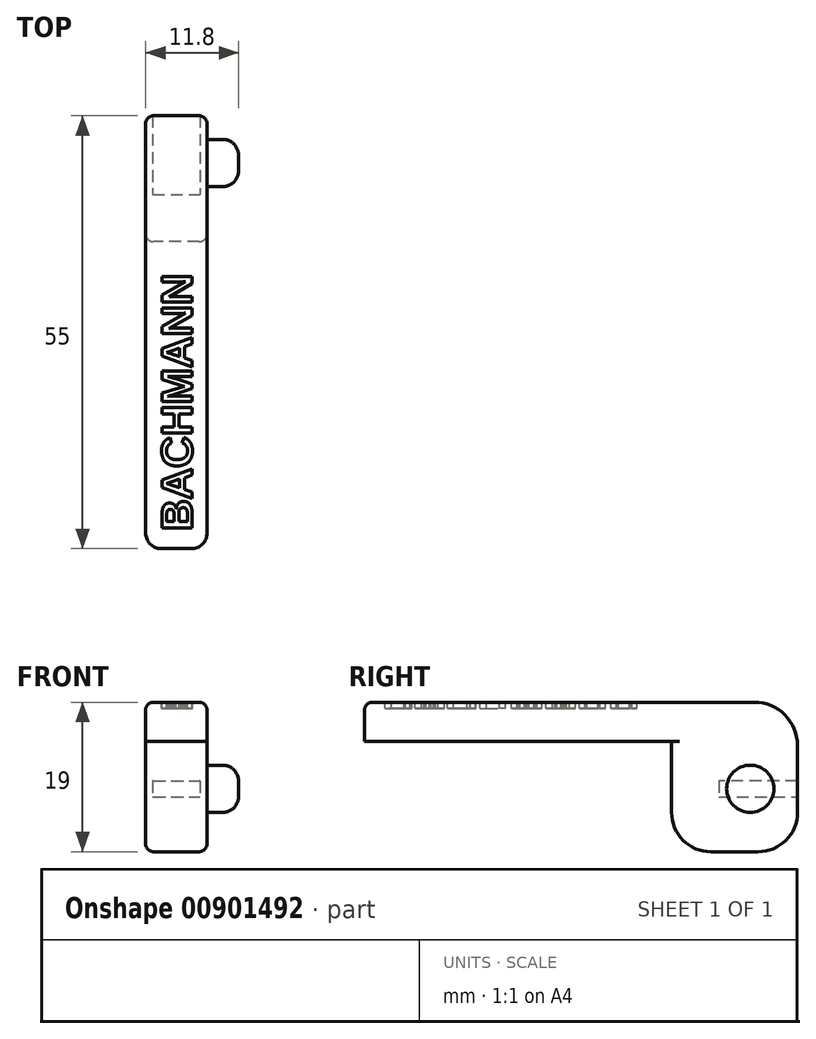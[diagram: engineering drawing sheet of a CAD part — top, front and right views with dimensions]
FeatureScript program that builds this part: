
annotation { "Feature Type Name" : "Feature", "Feature Type Description" : "" }
export const myFeature = defineFeature(function(context is Context, id is Id, definition is map)
    precondition{}
    {
        {
            var Q0;
            Q0=qCreatedBy(makeId("Right.planeOp"),FACE);
            var sketch = newSketch(context, id + "F0", { "sketchPlane" : qUnion([Q0])});
            skLineSegment(sketch, "E0", {"start": v(0, 0) * mm, "end": v(39, 0) * mm});
            skLineSegment(sketch, "E1", {"start": v(39, 0) * mm, "end": v(0, 0) * mm});
            skLineSegment(sketch, "E2", {"start": v(0, 0) * mm, "end": v(0, 5) * mm});
            skLineSegment(sketch, "E3", {"start": v(0, 5) * mm, "end": v(55, 5) * mm});
            skLineSegment(sketch, "E4", {"start": v(55, 5) * mm, "end": v(55, -14) * mm});
            skLineSegment(sketch, "E5", {"start": v(55, -14) * mm, "end": v(39, -14) * mm});
            skLineSegment(sketch, "E6", {"start": v(39, -14) * mm, "end": v(39, 0) * mm});
            skSolve(sketch);
        }
        {
            var Q0;
            Q0 = qSketchRegion(id + "F0", true);
            extrude(context, id + "F1", {"entities" : qUnion([Q0]), "endBound" : BoundingType.SYMMETRIC, "depth" : 7.8 * mm, "offsetDistance" : 25 * mm});
        }
        {
            var Q0;
            Q0=qCreatedBy(makeId("Right.planeOp"),FACE);
            var sketch = newSketch(context, id + "F2", { "sketchPlane" : qUnion([Q0])});
            skLineSegment(sketch, "E7.0", {"start": v(55, 5) * mm, "end": v(55, -14) * mm});
            skLineSegment(sketch, "E8", {"start": v(55, -5) * mm, "end": v(45, -5) * mm});
            skLineSegment(sketch, "E9", {"start": v(45, -5) * mm, "end": v(45, -7) * mm});
            skLineSegment(sketch, "E10", {"start": v(45, -7) * mm, "end": v(55, -7) * mm});
            skSolve(sketch);
        }
        {
            var Q0;
            Q0 = qSketchRegion(id + "F2", true);
            extrude(context, id + "F3", {"entities" : qUnion([Q0]), "operationType" : NewBodyOperationType.REMOVE, "endBound" : BoundingType.SYMMETRIC, "oppositeDirection" : true, "depth" : 6 * mm, "offsetDistance" : 25 * mm});
        }
        {
            var Q0;
            Q0=makeQuery(id+"F1.opExtrude","SWEPT_FACE",FACE,{"disambiguationData":[OSD([sQuery(id+"F0.wireOp",EDGE,"E3")])]});
            var sketch = newSketch(context, id + "F4", { "sketchPlane" : qUnion([Q0])});
            skText(sketch, "E11", { "text": "BACHMANN", "fontName": "Arimo-Bold.ttf"});
            const initialGuessF4  = {"E11": [0.002, 0.00226, 0, 1, 0.004]};
            skSetInitialGuess(sketch, initialGuessF4);
            skSolve(sketch);
        }
        {
            var Q0;
            Q0=makeQuery(id+"F1.opExtrude","CAP_FACE",FACE,{"disambiguationData":[OSD([sQuery(id+"F0.wireOp",EDGE,"E1"),sQuery(id+"F0.wireOp",EDGE,"E2"),sQuery(id+"F0.wireOp",EDGE,"E3"),sQuery(id+"F0.wireOp",EDGE,"E4"),sQuery(id+"F0.wireOp",EDGE,"E5"),sQuery(id+"F0.wireOp",EDGE,"E6")])],"isStart":false});
            var sketch = newSketch(context, id + "F5", { "sketchPlane" : qUnion([Q0])});
            skCircle(sketch, "E12", {"center": v(49, -6) * mm, "radius": 3 * mm});
            skSolve(sketch);
        }
        {
            var Q0;
            Q0 = qSketchRegion(id + "F5", true);
            extrude(context, id + "F6", {"entities" : qUnion([Q0]), "operationType" : NewBodyOperationType.ADD, "depth" : 4 * mm, "offsetDistance" : 25 * mm});
        }
        {
            var Q0;
            Q0 = qSketchRegion(id + "F4", true);
            extrude(context, id + "F7", {"entities" : qUnion([Q0]), "operationType" : NewBodyOperationType.REMOVE, "oppositeDirection" : true, "depth" : .8 * mm, "offsetDistance" : 25 * mm});
        }
        {
            var Q0;
            {var subQ0=sQuery(id+"F0.wireOp",EDGE,"E2");var subQ4=sQuery(id+"F0.wireOp",EDGE,"E3");Q0=makeQuery(id+"F7.boolean.opBoolean","SPLIT",FACE,{"disambiguationData":[TD([makeQuery(id+"F1.opExtrude","SWEPT_FACE",FACE,{"disambiguationData":[OSD([subQ0])]})])],"derivedFrom":makeQuery(id+"F1.opExtrude","SWEPT_FACE",FACE,{"disambiguationData":[OSD([subQ4])]})});}
            var sketch = newSketch(context, id + "F8", { "sketchPlane" : qUnion([Q0])});
            skText(sketch, "E13", { "text": "BACH", "fontName": "DroidSansMono.ttf"});
            skText(sketch, "E14", { "text": "MANN", "fontName": "DroidSansMono.ttf"});
            const initialGuessF8  = {"E13": [-0.0035, 0.04297, 1, 0, 0.00203], "E14": [-0.0035, 0.03994, 1, 0, 0.00203]};
            skSetInitialGuess(sketch, initialGuessF8);
            skSolve(sketch);
        }
        {
            var Q0;
            Q0=makeQuery(id+"F1.opExtrude","SWEPT_EDGE",EDGE,{"disambiguationData":[OSD([sQuery(id+"F0.wireOp",EDGE,"E3"),sQuery(id+"F0.wireOp",EDGE,"E4")])]});
            fillet(context, id + "F9", {"entities" : qUnion([Q0]), "radius" : 5.5 * mm, "tangentPropagation" : true, "allowEdgeOverflow" : false});
        }
        {
            var Q0;
            Q0=makeQuery(id+"F1.opExtrude","SWEPT_EDGE",EDGE,{"disambiguationData":[OSD([sQuery(id+"F0.wireOp",EDGE,"E5"),sQuery(id+"F0.wireOp",EDGE,"E6")])]});
            fillet(context, id + "F10", {"entities" : qUnion([Q0]), "radius" : 5 * mm, "tangentPropagation" : true, "allowEdgeOverflow" : false});
        }
        {
            var Q0;
            Q0=makeQuery(id+"F1.opExtrude","CAP_EDGE",EDGE,{"disambiguationData":[OSD([sQuery(id+"F0.wireOp",EDGE,"E2")])],"isStart":false});
            var Q1;
            Q1=makeQuery(id+"F1.opExtrude","CAP_EDGE",EDGE,{"disambiguationData":[OSD([sQuery(id+"F0.wireOp",EDGE,"E2")])],"isStart":true});
            fillet(context, id + "F11", {"entities" : qUnion([Q0, Q1]), "radius" : 2 * mm, "tangentPropagation" : true, "allowEdgeOverflow" : false});
        }
        {
            var Q0;
            Q0=makeQuery(id+"F1.opExtrude","SWEPT_EDGE",EDGE,{"disambiguationData":[OSD([sQuery(id+"F0.wireOp",EDGE,"E4"),sQuery(id+"F0.wireOp",EDGE,"E5")])]});
            fillet(context, id + "F12", {"entities" : qUnion([Q0]), "radius" : 5 * mm, "tangentPropagation" : true, "allowEdgeOverflow" : false});
        }
        {
            var Q0;
            Q0=makeQuery(id+"F1.opExtrude","CAP_EDGE",EDGE,{"disambiguationData":[OSD([sQuery(id+"F0.wireOp",EDGE,"E3")])],"isStart":false});
            var Q1;
            {var subQ1=sQuery(id+"F0.wireOp",EDGE,"E2");var subQ4=sQuery(id+"F0.wireOp",EDGE,"E3");Q1=makeQuery(id+"F11.opFillet","BLEND_EDGE",EDGE,{"blendedFrom":[makeQuery(id+"F1.opExtrude","CAP_EDGE",EDGE,{"disambiguationData":[OSD([subQ1])],"isStart":false}),makeQuery(id+"F7.boolean.opBoolean","SPLIT",FACE,{"disambiguationData":[TD([makeQuery(id+"F1.opExtrude","SWEPT_FACE",FACE,{"disambiguationData":[OSD([subQ1])]})])],"derivedFrom":makeQuery(id+"F1.opExtrude","SWEPT_FACE",FACE,{"disambiguationData":[OSD([subQ4])]})})],"blendedInto":[makeQuery(id+"F7.boolean.opBoolean","SPLIT",FACE,{"disambiguationData":[TD([makeQuery(id+"F1.opExtrude","SWEPT_FACE",FACE,{"disambiguationData":[OSD([subQ1])]})])],"derivedFrom":makeQuery(id+"F1.opExtrude","SWEPT_FACE",FACE,{"disambiguationData":[OSD([subQ4])]})})]});}
            var Q2;
            Q2=makeQuery(id+"F1.opExtrude","SWEPT_EDGE",EDGE,{"disambiguationData":[OSD([sQuery(id+"F0.wireOp",EDGE,"E2"),sQuery(id+"F0.wireOp",EDGE,"E3")])]});
            var Q3;
            {var subQ1=sQuery(id+"F0.wireOp",EDGE,"E2");var subQ4=sQuery(id+"F0.wireOp",EDGE,"E3");Q3=makeQuery(id+"F11.opFillet","BLEND_EDGE",EDGE,{"blendedFrom":[makeQuery(id+"F1.opExtrude","CAP_EDGE",EDGE,{"disambiguationData":[OSD([subQ1])],"isStart":true}),makeQuery(id+"F7.boolean.opBoolean","SPLIT",FACE,{"disambiguationData":[TD([makeQuery(id+"F1.opExtrude","SWEPT_FACE",FACE,{"disambiguationData":[OSD([subQ1])]})])],"derivedFrom":makeQuery(id+"F1.opExtrude","SWEPT_FACE",FACE,{"disambiguationData":[OSD([subQ4])]})})],"blendedInto":[makeQuery(id+"F7.boolean.opBoolean","SPLIT",FACE,{"disambiguationData":[TD([makeQuery(id+"F1.opExtrude","SWEPT_FACE",FACE,{"disambiguationData":[OSD([subQ1])]})])],"derivedFrom":makeQuery(id+"F1.opExtrude","SWEPT_FACE",FACE,{"disambiguationData":[OSD([subQ4])]})})]});}
            var Q4;
            Q4=makeQuery(id+"F1.opExtrude","CAP_EDGE",EDGE,{"disambiguationData":[OSD([sQuery(id+"F0.wireOp",EDGE,"E3")])],"isStart":true});
            fillet(context, id + "F13", {"entities" : qUnion([Q0, Q1, Q2, Q3, Q4]), "radius" : 1 * mm, "tangentPropagation" : true, "allowEdgeOverflow" : false});
        }
        {
            var Q0;
            Q0=makeQuery(id+"F6.opExtrude","CAP_EDGE",EDGE,{"disambiguationData":[OSD([sQuery(id+"F5.wireOp",EDGE,"E12")])],"isStart":false});
            fillet(context, id + "F14", {"entities" : qUnion([Q0]), "radius" : 2 * mm, "tangentPropagation" : true, "allowEdgeOverflow" : false});
        }
    });
